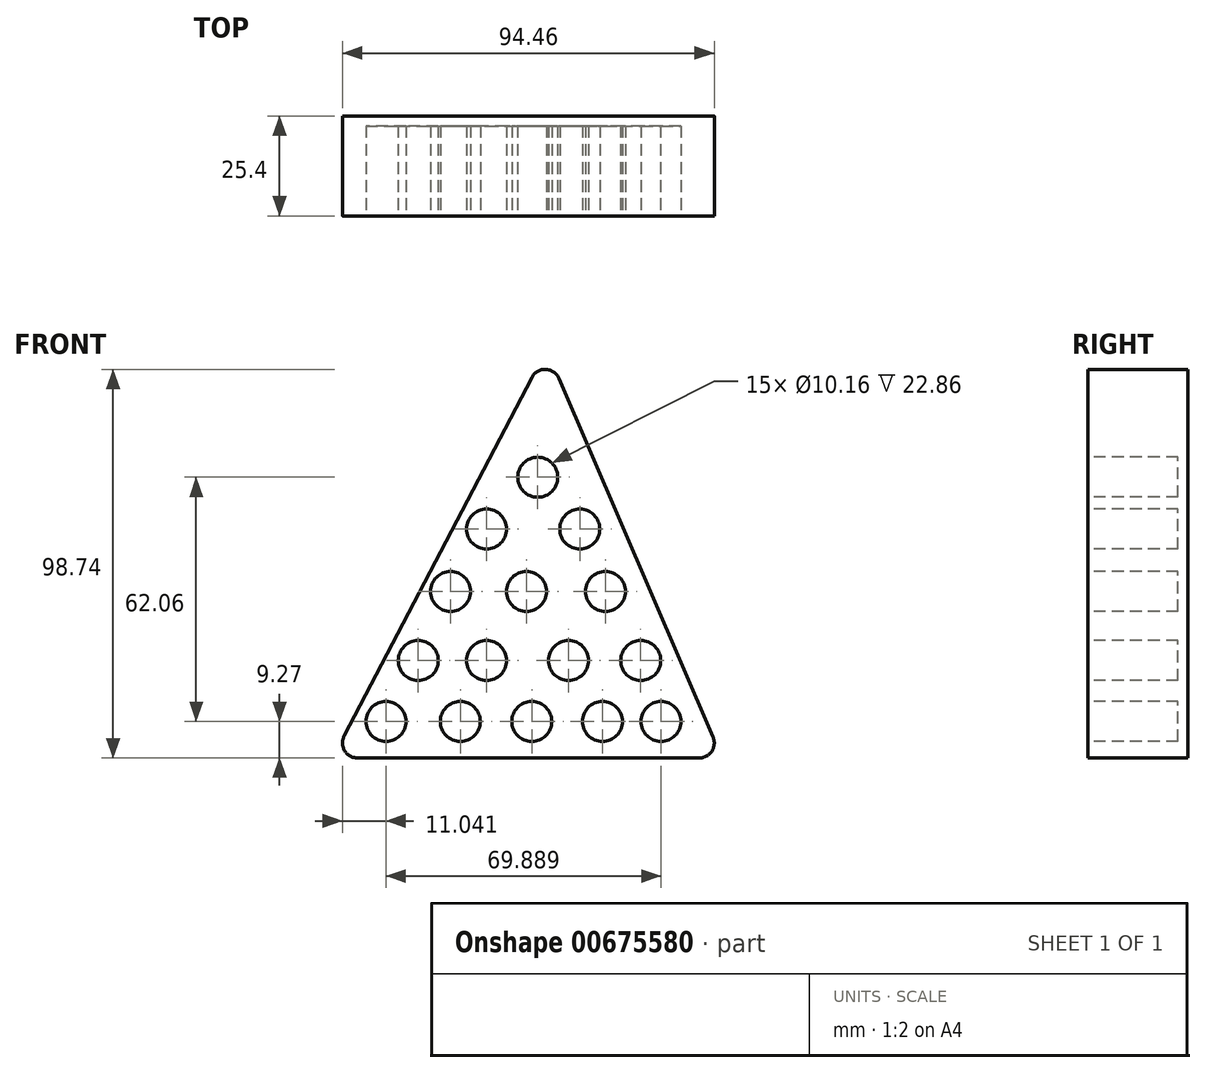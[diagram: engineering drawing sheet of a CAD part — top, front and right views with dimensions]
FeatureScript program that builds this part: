
annotation { "Feature Type Name" : "Feature", "Feature Type Description" : "" }
export const myFeature = defineFeature(function(context is Context, id is Id, definition is map)
    precondition{}
    {
        {
            var Q0;
            Q0=qCreatedBy(makeId("Front.planeOp"),FACE);
            var sketch = newSketch(context, id + "F0", { "sketchPlane" : qUnion([Q0])});
            skLineSegment(sketch, "E0", {"start": v(-3.71, 68.43) * mm, "end": v(-51.37, -22.7) * mm});
            skLineSegment(sketch, "E1", {"start": v(-48, -28.27) * mm, "end": v(38.84, -28.27) * mm});
            skLineSegment(sketch, "E2", {"start": v(42.34, -22.95) * mm, "end": v(3.16, 68.16) * mm});
            skPoint(sketch, "E3.visualSharp", {"position": v(-54.3, -28.27) * mm});
            skArc(sketch, "E3.filletArc", {"start": v(-51.37, -22.7) * mm, "mid": v(-51.26, -26.43) * mm, "end": v(-48, -28.27) * mm});
            skPoint(sketch, "E4.visualSharp", {"position": v(44.63, -28.27) * mm});
            skArc(sketch, "E4.filletArc", {"start": v(38.84, -28.27) * mm, "mid": v(42.03, -26.55) * mm, "end": v(42.34, -22.95) * mm});
            skPoint(sketch, "E5.visualSharp", {"position": v(0, 75.52) * mm});
            skArc(sketch, "E5.filletArc", {"start": v(3.16, 68.16) * mm, "mid": v(-0.2, 70.47) * mm, "end": v(-3.71, 68.43) * mm});
            skSolve(sketch);
        }
        {
            var Q0;
            Q0=makeQuery(id+"F0.imprint","IMPRINT",FACE,{"disambiguationData":[TD([[makeQuery(id+"F0.imprint","IMPRINT",EDGE,{"derivedFrom":sQuery(id+"F0.wireOp",EDGE,"E0")}),1.0]])]});
            extrude(context, id + "F1", {"entities" : qUnion([Q0]), "depth" : 25.4 * mm, "offsetDistance" : 25.4 * mm});
        }
        {
            var Q0;
            Q0=makeQuery(id+"F1.opExtrude","CAP_FACE",FACE,{"disambiguationData":[OSD([sQuery(id+"F0.wireOp",EDGE,"E0"),sQuery(id+"F0.wireOp",EDGE,"E1"),sQuery(id+"F0.wireOp",EDGE,"E2"),sQuery(id+"F0.wireOp",EDGE,"E3.filletArc"),sQuery(id+"F0.wireOp",EDGE,"E4.filletArc"),sQuery(id+"F0.wireOp",EDGE,"E5.filletArc")])],"isStart":false});
            var sketch = newSketch(context, id + "F2", { "sketchPlane" : qUnion([Q0])});
            skCircle(sketch, "E6", {"center": v(-40.77, -19) * mm, "radius": 5.08 * mm});
            skCircle(sketch, "E7", {"center": v(-21.86, -19) * mm, "radius": 5.08 * mm});
            skCircle(sketch, "E8", {"center": v(-3.71, -19) * mm, "radius": 5.08 * mm});
            skCircle(sketch, "E9", {"center": v(14.23, -19) * mm, "radius": 5.08 * mm});
            skCircle(sketch, "E10", {"center": v(29.12, -19) * mm, "radius": 5.08 * mm});
            skCircle(sketch, "E11", {"center": v(-2.2, 43.06) * mm, "radius": 5.08 * mm});
            skCircle(sketch, "E12", {"center": v(-15.18, 29.88) * mm, "radius": 5.08 * mm});
            skCircle(sketch, "E13", {"center": v(8.5, 29.88) * mm, "radius": 5.08 * mm});
            skCircle(sketch, "E14", {"center": v(-32.56, -3.53) * mm, "radius": 5.08 * mm});
            skCircle(sketch, "E15", {"center": v(-15.18, -3.53) * mm, "radius": 5.08 * mm});
            skCircle(sketch, "E16", {"center": v(5.63, -3.53) * mm, "radius": 5.08 * mm});
            skCircle(sketch, "E17", {"center": v(23.96, -3.53) * mm, "radius": 5.08 * mm});
            skCircle(sketch, "E18", {"center": v(-24.35, 14.04) * mm, "radius": 5.08 * mm});
            skCircle(sketch, "E19", {"center": v(-5.06, 14.04) * mm, "radius": 5.08 * mm});
            skCircle(sketch, "E20", {"center": v(14.99, 14.04) * mm, "radius": 5.08 * mm});
            skSolve(sketch);
        }
        {
            var Q0;
            Q0=makeQuery(id+"F2.imprint","IMPRINT",FACE,{"disambiguationData":[TD([[makeQuery(id+"F2.imprint","IMPRINT",EDGE,{"derivedFrom":sQuery(id+"F2.wireOp",EDGE,"E18")}),1.0]])]});
            var Q1;
            Q1=makeQuery(id+"F2.imprint","IMPRINT",FACE,{"disambiguationData":[TD([[makeQuery(id+"F2.imprint","IMPRINT",EDGE,{"derivedFrom":sQuery(id+"F2.wireOp",EDGE,"E12")}),1.0]])]});
            var Q2;
            Q2=makeQuery(id+"F2.imprint","IMPRINT",FACE,{"disambiguationData":[TD([[makeQuery(id+"F2.imprint","IMPRINT",EDGE,{"derivedFrom":sQuery(id+"F2.wireOp",EDGE,"E11")}),1.0]])]});
            var Q3;
            Q3=makeQuery(id+"F2.imprint","IMPRINT",FACE,{"disambiguationData":[TD([[makeQuery(id+"F2.imprint","IMPRINT",EDGE,{"derivedFrom":sQuery(id+"F2.wireOp",EDGE,"E8")}),1.0]])]});
            var Q4;
            Q4=makeQuery(id+"F2.imprint","IMPRINT",FACE,{"disambiguationData":[TD([[makeQuery(id+"F2.imprint","IMPRINT",EDGE,{"derivedFrom":sQuery(id+"F2.wireOp",EDGE,"E9")}),1.0]])]});
            var Q5;
            Q5=makeQuery(id+"F2.imprint","IMPRINT",FACE,{"disambiguationData":[TD([[makeQuery(id+"F2.imprint","IMPRINT",EDGE,{"derivedFrom":sQuery(id+"F2.wireOp",EDGE,"E10")}),1.0]])]});
            var Q6;
            Q6=makeQuery(id+"F2.imprint","IMPRINT",FACE,{"disambiguationData":[TD([[makeQuery(id+"F2.imprint","IMPRINT",EDGE,{"derivedFrom":sQuery(id+"F2.wireOp",EDGE,"E7")}),1.0]])]});
            var Q7;
            Q7=makeQuery(id+"F2.imprint","IMPRINT",FACE,{"disambiguationData":[TD([[makeQuery(id+"F2.imprint","IMPRINT",EDGE,{"derivedFrom":sQuery(id+"F2.wireOp",EDGE,"E6")}),1.0]])]});
            var Q8;
            Q8=makeQuery(id+"F2.imprint","IMPRINT",FACE,{"disambiguationData":[TD([[makeQuery(id+"F2.imprint","IMPRINT",EDGE,{"derivedFrom":sQuery(id+"F2.wireOp",EDGE,"E14")}),1.0]])]});
            var Q9;
            Q9=makeQuery(id+"F2.imprint","IMPRINT",FACE,{"disambiguationData":[TD([[makeQuery(id+"F2.imprint","IMPRINT",EDGE,{"derivedFrom":sQuery(id+"F2.wireOp",EDGE,"E15")}),1.0]])]});
            var Q10;
            Q10=makeQuery(id+"F2.imprint","IMPRINT",FACE,{"disambiguationData":[TD([[makeQuery(id+"F2.imprint","IMPRINT",EDGE,{"derivedFrom":sQuery(id+"F2.wireOp",EDGE,"E16")}),1.0]])]});
            var Q11;
            Q11=makeQuery(id+"F2.imprint","IMPRINT",FACE,{"disambiguationData":[TD([[makeQuery(id+"F2.imprint","IMPRINT",EDGE,{"derivedFrom":sQuery(id+"F2.wireOp",EDGE,"E17")}),1.0]])]});
            var Q12;
            Q12=makeQuery(id+"F2.imprint","IMPRINT",FACE,{"disambiguationData":[TD([[makeQuery(id+"F2.imprint","IMPRINT",EDGE,{"derivedFrom":sQuery(id+"F2.wireOp",EDGE,"E20")}),1.0]])]});
            var Q13;
            Q13=makeQuery(id+"F2.imprint","IMPRINT",FACE,{"disambiguationData":[TD([[makeQuery(id+"F2.imprint","IMPRINT",EDGE,{"derivedFrom":sQuery(id+"F2.wireOp",EDGE,"E19")}),1.0]])]});
            var Q14;
            Q14=makeQuery(id+"F2.imprint","IMPRINT",FACE,{"disambiguationData":[TD([[makeQuery(id+"F2.imprint","IMPRINT",EDGE,{"derivedFrom":sQuery(id+"F2.wireOp",EDGE,"E13")}),1.0]])]});
            extrude(context, id + "F3", {"entities" : qUnion([Q0, Q1, Q2, Q3, Q4, Q5, Q6, Q7, Q8, Q9, Q10, Q11, Q12, Q13, Q14]), "operationType" : NewBodyOperationType.REMOVE, "oppositeDirection" : true, "depth" : 22.86 * mm, "offsetDistance" : 25.4 * mm});
        }
    });
